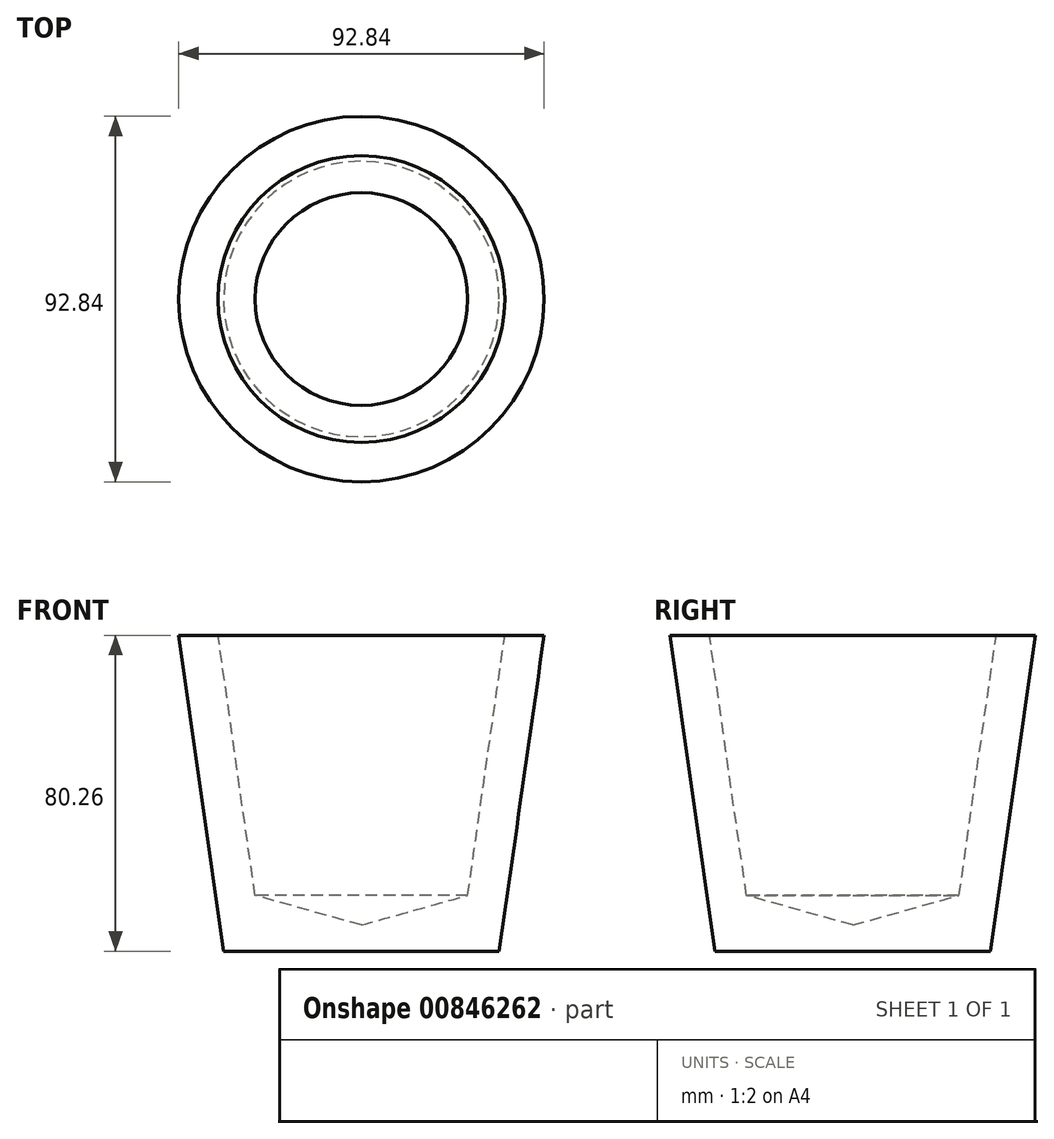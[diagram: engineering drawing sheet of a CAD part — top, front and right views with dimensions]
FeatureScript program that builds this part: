
annotation { "Feature Type Name" : "Feature", "Feature Type Description" : "" }
export const myFeature = defineFeature(function(context is Context, id is Id, definition is map)
    precondition{}
    {
        {
            var Q0;
            Q0=qCreatedBy(makeId("Front.planeOp"),FACE);
            var sketch = newSketch(context, id + "F0", { "sketchPlane" : qUnion([Q0])});
            skLineSegment(sketch, "E0", {"start": v(0, 0) * mm, "end": v(-35, 0) * mm});
            skLineSegment(sketch, "E1", {"start": v(-35, 0) * mm, "end": v(-46.42, 80.26) * mm});
            skLineSegment(sketch, "E2", {"start": v(-46.42, 80.26) * mm, "end": v(-36.42, 80.26) * mm});
            skLineSegment(sketch, "E3", {"start": v(-36.42, 80.26) * mm, "end": v(-27.02, 14.18) * mm});
            skLineSegment(sketch, "E4", {"start": v(-27.02, 14.18) * mm, "end": v(0, 6.63) * mm});
            skLineSegment(sketch, "E5", {"start": v(0, 6.63) * mm, "end": v(0, 0) * mm});
            skSolve(sketch);
        }
        {
            var Q0;
            Q0 = qSketchRegion(id + "F0", true);
            var Q1;
            Q1=sQuery(id+"F0.wireOp",EDGE,"E5");
            revolve(context, id + "F1", {"surfaceOperationType" : NewSurfaceOperationType.NEW, "entities" : qUnion([Q0]), "axis" : qUnion([Q1]), "revolveType" : RevolveType.FULL});
        }
    });
